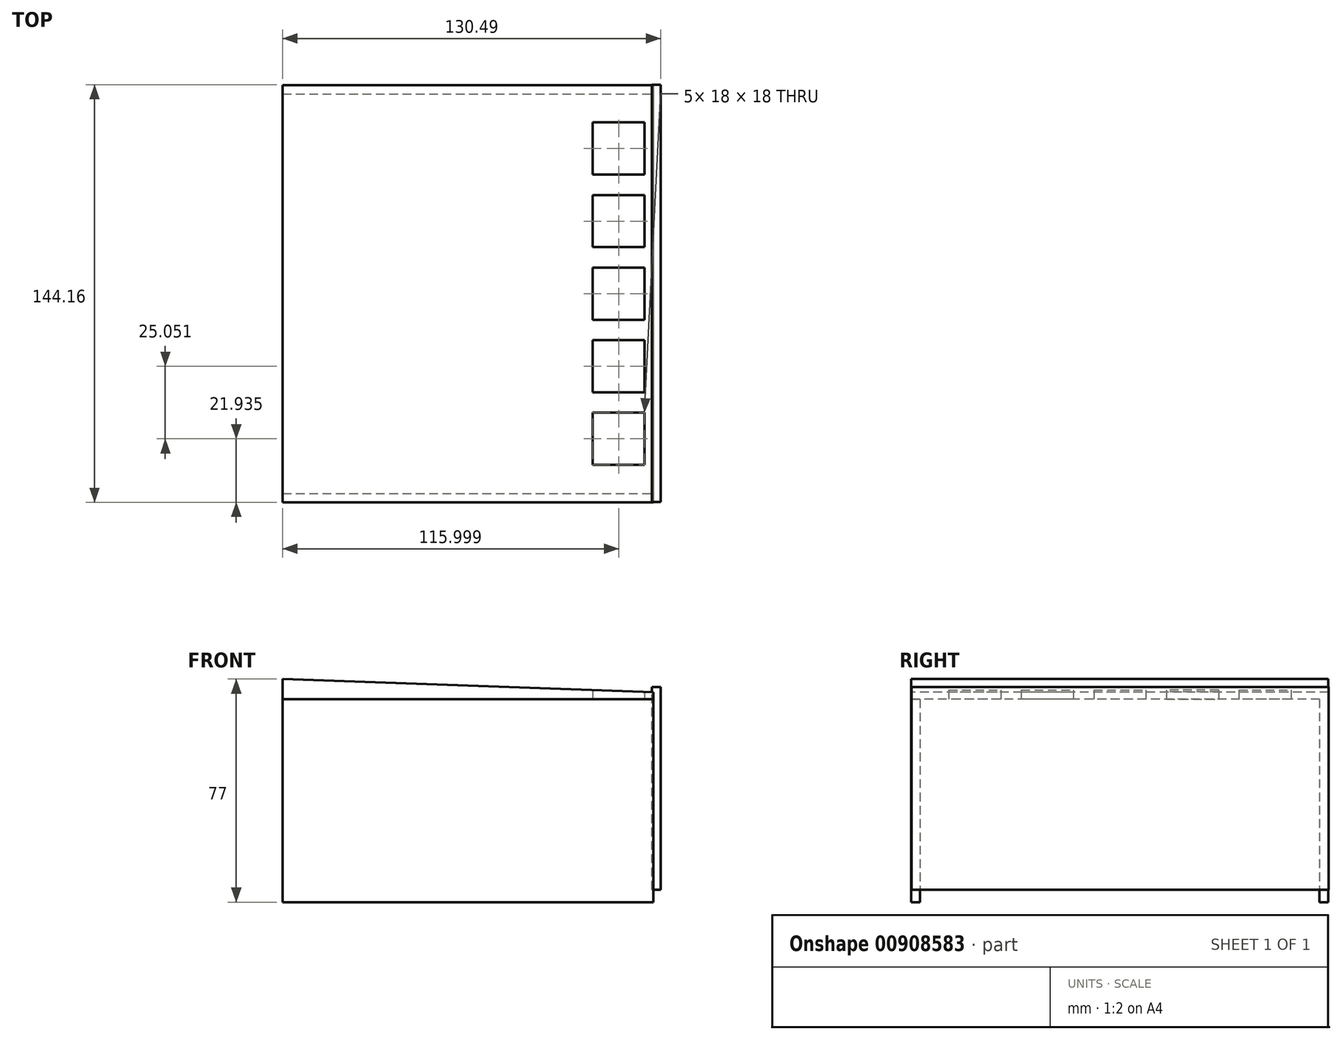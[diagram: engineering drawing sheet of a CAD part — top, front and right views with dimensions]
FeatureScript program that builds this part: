
annotation { "Feature Type Name" : "Feature", "Feature Type Description" : "" }
export const myFeature = defineFeature(function(context is Context, id is Id, definition is map)
    precondition{}
    {
        {
            var Q0;
            Q0=qCreatedBy(makeId("Top.planeOp"),FACE);
            var sketch = newSketch(context, id + "F0", { "sketchPlane" : qUnion([Q0])});
            skLineSegment(sketch, "E0.bottom", {"start": v(-72.5, 99.04) * mm, "end": v(52.5, 99.04) * mm});
            skLineSegment(sketch, "E0.top", {"start": v(-72.5, -44.96) * mm, "end": v(52.5, -44.96) * mm});
            skLineSegment(sketch, "E0.left", {"start": v(-72.5, 99.04) * mm, "end": v(-72.5, -44.96) * mm});
            skLineSegment(sketch, "E1.bottom", {"start": v(52.5, 86.14) * mm, "end": v(34.5, 86.14) * mm});
            skLineSegment(sketch, "E1.top", {"start": v(52.5, 68.14) * mm, "end": v(34.5, 68.14) * mm});
            skLineSegment(sketch, "E1.left", {"start": v(52.5, 86.14) * mm, "end": v(52.5, 68.14) * mm});
            skLineSegment(sketch, "E1.right", {"start": v(34.5, 86.14) * mm, "end": v(34.5, 68.14) * mm});
            skLineSegment(sketch, "E2.bottom", {"start": v(52.5, 43.09) * mm, "end": v(52.5, 61.09) * mm});
            skLineSegment(sketch, "E2.top", {"start": v(34.5, 43.09) * mm, "end": v(34.5, 61.09) * mm});
            skLineSegment(sketch, "E2.left", {"start": v(52.5, 43.09) * mm, "end": v(34.5, 43.09) * mm});
            skLineSegment(sketch, "E2.right", {"start": v(52.5, 61.09) * mm, "end": v(34.5, 61.09) * mm});
            skLineSegment(sketch, "E3.bottom", {"start": v(52.5, 36.04) * mm, "end": v(34.5, 36.04) * mm});
            skLineSegment(sketch, "E3.top", {"start": v(52.5, 18.04) * mm, "end": v(34.5, 18.04) * mm});
            skLineSegment(sketch, "E3.left", {"start": v(52.5, 36.04) * mm, "end": v(52.5, 18.04) * mm});
            skLineSegment(sketch, "E3.right", {"start": v(34.5, 36.04) * mm, "end": v(34.5, 18.04) * mm});
            skLineSegment(sketch, "E4.bottom", {"start": v(52.5, 10.99) * mm, "end": v(34.5, 10.99) * mm});
            skLineSegment(sketch, "E4.top", {"start": v(52.5, -7.01) * mm, "end": v(34.5, -7.01) * mm});
            skLineSegment(sketch, "E4.left", {"start": v(52.5, 10.99) * mm, "end": v(52.5, -7.01) * mm});
            skLineSegment(sketch, "E4.right", {"start": v(34.5, 10.99) * mm, "end": v(34.5, -7.01) * mm});
            skLineSegment(sketch, "E5.bottom", {"start": v(52.5, -14.06) * mm, "end": v(34.5, -14.06) * mm});
            skLineSegment(sketch, "E5.top", {"start": v(52.5, -32.06) * mm, "end": v(34.5, -32.06) * mm});
            skLineSegment(sketch, "E5.left", {"start": v(52.5, -14.06) * mm, "end": v(52.5, -32.06) * mm});
            skLineSegment(sketch, "E5.right", {"start": v(34.5, -14.06) * mm, "end": v(34.5, -32.06) * mm});
            skLineSegment(sketch, "E6", {"start": v(52.5, -14.06) * mm, "end": v(52.5, -7.01) * mm});
            skLineSegment(sketch, "E7", {"start": v(52.5, 10.99) * mm, "end": v(52.5, 18.04) * mm});
            skLineSegment(sketch, "E8", {"start": v(52.5, 36.04) * mm, "end": v(52.5, 43.09) * mm});
            skLineSegment(sketch, "E9", {"start": v(52.5, 61.09) * mm, "end": v(52.5, 68.14) * mm});
            skLineSegment(sketch, "E10", {"start": v(52.5, 99.04) * mm, "end": v(55.5, 99.04) * mm});
            skLineSegment(sketch, "E11", {"start": v(55.5, 99.04) * mm, "end": v(55.5, -44.96) * mm});
            skLineSegment(sketch, "E12", {"start": v(55.5, -44.96) * mm, "end": v(52.5, -44.96) * mm});
            skLineSegment(sketch, "E13", {"start": v(34.63, 99.04) * mm, "end": v(34.63, -44.96) * mm, "construction": true});
            skSolve(sketch);
        }
        {
            var Q0;
            Q0=qCreatedBy(makeId("Front.planeOp"),FACE);
            var sketch = newSketch(context, id + "F1", { "sketchPlane" : qUnion([Q0])});
            skLineSegment(sketch, "E14.bottom", {"start": v(-72.5, 0) * mm, "end": v(55.5, 0) * mm});
            skLineSegment(sketch, "E14.top", {"start": v(-72.5, -70) * mm, "end": v(55.5, -70) * mm});
            skLineSegment(sketch, "E14.left", {"start": v(-72.5, 0) * mm, "end": v(-72.5, -70) * mm});
            skLineSegment(sketch, "E14.right", {"start": v(55.5, 0) * mm, "end": v(55.5, -70) * mm});
            skSolve(sketch);
        }
        {
            var Q0;
            Q0=qCreatedBy(makeId("Right.planeOp"),FACE);
            var sketch = newSketch(context, id + "F2", { "sketchPlane" : qUnion([Q0])});
            skLineSegment(sketch, "E15.bottom", {"start": v(-44.84, -65.7) * mm, "end": v(99.16, -65.7) * mm});
            skLineSegment(sketch, "E15.top", {"start": v(-44.84, 4.3) * mm, "end": v(99.16, 4.3) * mm});
            skLineSegment(sketch, "E15.left", {"start": v(-44.84, -65.7) * mm, "end": v(-44.84, 4.3) * mm});
            skLineSegment(sketch, "E15.right", {"start": v(99.16, -65.7) * mm, "end": v(99.16, 4.3) * mm});
            skSolve(sketch);
        }
        {
            var Q0;
            Q0 = qSketchRegion(id + "F0", true);
            extrude(context, id + "F3", {"entities" : qUnion([Q0]), "depth" : 7 * mm, "offsetDistance" : 25 * mm});
        }
        {
            var Q0;
            Q0=makeQuery(id+"F3.opExtrude","CAP_EDGE",EDGE,{"disambiguationData":[OSD([sQuery(id+"F0.wireOp",EDGE,"E11")])],"isStart":false});
            chamfer(context, id + "F4", {"entities" : qUnion([Q0]), "chamferType" : ChamferType.OFFSET_ANGLE, "width" : 128 * mm, "oppositeDirection" : true, "angle" : 2 * degree});
        }
        {
            var Q0;
            Q0 = qSketchRegion(id + "F1", true);
            extrude(context, id + "F5", {"entities" : qUnion([Q0]), "depth" : 45 * mm, "offsetDistance" : 25 * mm, "hasSecondDirection" : true, "secondDirectionOppositeDirection" : false, "secondDirectionDepth" : 42 * mm});
        }
        {
            var Q0;
            Q0 = qSketchRegion(id + "F1", true);
            extrude(context, id + "F6", {"entities" : qUnion([Q0]), "operationType" : NewBodyOperationType.ADD, "oppositeDirection" : true, "depth" : 99 * mm, "offsetDistance" : 25 * mm, "hasSecondDirection" : true, "secondDirectionOppositeDirection" : true, "secondDirectionDepth" : 96 * mm});
        }
        {
            var Q0;
            Q0 = qSketchRegion(id + "F2", true);
            extrude(context, id + "F7", {"entities" : qUnion([Q0]), "depth" : 58 * mm, "offsetDistance" : 25 * mm, "hasSecondDirection" : true, "secondDirectionOppositeDirection" : false, "secondDirectionDepth" : 55 * mm});
        }
    });
